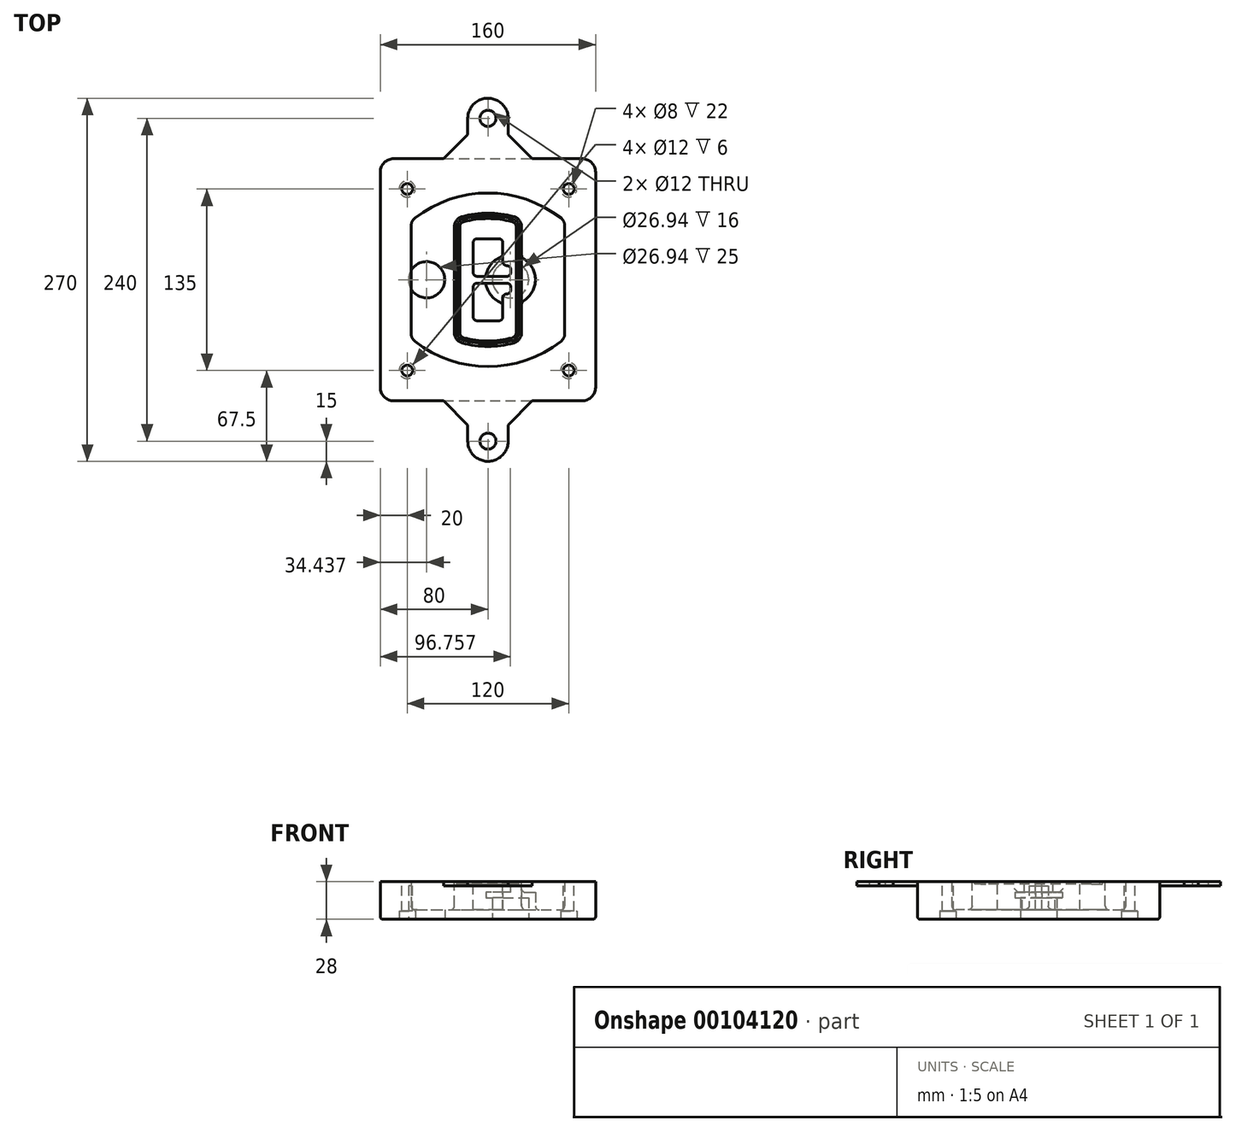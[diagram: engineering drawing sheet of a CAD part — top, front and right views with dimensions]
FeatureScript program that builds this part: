
annotation { "Feature Type Name" : "Feature", "Feature Type Description" : "" }
export const myFeature = defineFeature(function(context is Context, id is Id, definition is map)
    precondition{}
    {
        {
            var Q0;
            Q0=qCreatedBy(makeId("Top.planeOp"),FACE);
            var sketch = newSketch(context, id + "F0", { "sketchPlane" : qUnion([Q0])});
            skPoint(sketch, "E0.rect.middle", {"position": v(0, 0) * mm});
            skLineSegment(sketch, "E1.bottom", {"start": v(-70, -90) * mm, "end": v(70, -90) * mm});
            skLineSegment(sketch, "E1.top", {"start": v(-70, 90) * mm, "end": v(70, 90) * mm});
            skLineSegment(sketch, "E1.left", {"start": v(-80, -80) * mm, "end": v(-80, 80) * mm});
            skLineSegment(sketch, "E1.right", {"start": v(80, -80) * mm, "end": v(80, 80) * mm});
            skLineSegment(sketch, "E2", {"start": v(-80, 90) * mm, "end": v(80, -90) * mm, "construction": true});
            skLineSegment(sketch, "E3", {"start": v(80, 90) * mm, "end": v(-80, -90) * mm, "construction": true});
            skCircle(sketch, "E4", {"center": v(-60, 67.5) * mm, "radius": 4 * mm});
            skCircle(sketch, "E5", {"center": v(60, 67.5) * mm, "radius": 4 * mm});
            skCircle(sketch, "E6", {"center": v(60, -67.5) * mm, "radius": 4 * mm});
            skCircle(sketch, "E7", {"center": v(-60, -67.5) * mm, "radius": 4 * mm});
            skLineSegment(sketch, "E8", {"start": v(-60, 67.5) * mm, "end": v(60, 67.5) * mm, "construction": true});
            skLineSegment(sketch, "E9", {"start": v(60, 67.5) * mm, "end": v(60, -67.5) * mm, "construction": true});
            skLineSegment(sketch, "E10", {"start": v(60, -67.5) * mm, "end": v(-60, -67.5) * mm, "construction": true});
            skLineSegment(sketch, "E11", {"start": v(-60, -67.5) * mm, "end": v(-60, 67.5) * mm, "construction": true});
            skLineSegment(sketch, "E12", {"start": v(-60, 40.3) * mm, "end": v(-60, -40.3) * mm});
            skLineSegment(sketch, "E13", {"start": v(60, 40.3) * mm, "end": v(60, -40.3) * mm});
            skArc(sketch, "E14", {"start": v(56.15, 48.18) * mm, "mid": v(0, 67.5) * mm, "end": v(-56.15, 48.18) * mm});
            skArc(sketch, "E15", {"start": v(-56.15, -48.18) * mm, "mid": v(0, -67.5) * mm, "end": v(56.15, -48.18) * mm});
            skLineSegment(sketch, "E16", {"start": v(-60, 0) * mm, "end": v(60, 0) * mm, "construction": true});
            skPoint(sketch, "E17.visualSharp", {"position": v(-60, -45) * mm});
            skArc(sketch, "E17.filletArc", {"start": v(-60, -40.3) * mm, "mid": v(-58.99, -44.68) * mm, "end": v(-56.15, -48.18) * mm});
            skPoint(sketch, "E18.visualSharp", {"position": v(-60, 45) * mm});
            skArc(sketch, "E18.filletArc", {"start": v(-56.15, 48.18) * mm, "mid": v(-58.99, 44.68) * mm, "end": v(-60, 40.3) * mm});
            skPoint(sketch, "E19.visualSharp", {"position": v(60, 45) * mm});
            skArc(sketch, "E19.filletArc", {"start": v(60, 40.3) * mm, "mid": v(58.99, 44.68) * mm, "end": v(56.15, 48.18) * mm});
            skPoint(sketch, "E20.visualSharp", {"position": v(60, -45) * mm});
            skArc(sketch, "E20.filletArc", {"start": v(56.15, -48.18) * mm, "mid": v(58.99, -44.68) * mm, "end": v(60, -40.3) * mm});
            skPoint(sketch, "E21.visualSharp", {"position": v(-80, 90) * mm});
            skArc(sketch, "E21.filletArc", {"start": v(-70, 90) * mm, "mid": v(-77.07, 87.07) * mm, "end": v(-80, 80) * mm});
            skPoint(sketch, "E22.visualSharp", {"position": v(80, 90) * mm});
            skArc(sketch, "E22.filletArc", {"start": v(80, 80) * mm, "mid": v(77.07, 87.07) * mm, "end": v(70, 90) * mm});
            skPoint(sketch, "E23.visualSharp", {"position": v(80, -90) * mm});
            skArc(sketch, "E23.filletArc", {"start": v(70, -90) * mm, "mid": v(77.07, -87.07) * mm, "end": v(80, -80) * mm});
            skPoint(sketch, "E24.visualSharp", {"position": v(-80, -90) * mm});
            skArc(sketch, "E24.filletArc", {"start": v(-80, -80) * mm, "mid": v(-77.07, -87.07) * mm, "end": v(-70, -90) * mm});
            skArc(sketch, "E25.0", {"start": v(57, 40.3) * mm, "mid": v(56.3, 43.36) * mm, "end": v(54.3, 45.81) * mm});
            skLineSegment(sketch, "E25.1", {"start": v(57, 40.3) * mm, "end": v(57, -40.3) * mm});
            skArc(sketch, "E25.2", {"start": v(54.3, -45.81) * mm, "mid": v(56.3, -43.36) * mm, "end": v(57, -40.3) * mm});
            skArc(sketch, "E25.3", {"start": v(-54.3, -45.81) * mm, "mid": v(0, -64.5) * mm, "end": v(54.3, -45.81) * mm});
            skArc(sketch, "E25.4", {"start": v(-57, -40.3) * mm, "mid": v(-56.3, -43.36) * mm, "end": v(-54.3, -45.81) * mm});
            skArc(sketch, "E25.5", {"start": v(54.3, 45.81) * mm, "mid": v(0, 64.5) * mm, "end": v(-54.3, 45.81) * mm});
            skLineSegment(sketch, "E25.6", {"start": v(-57, 40.3) * mm, "end": v(-57, -40.3) * mm});
            skArc(sketch, "E25.7", {"start": v(-54.3, 45.81) * mm, "mid": v(-56.3, 43.36) * mm, "end": v(-57, 40.3) * mm});
            skArc(sketch, "E26.0", {"start": v(-58.62, 51.33) * mm, "mid": v(-62.58, 46.43) * mm, "end": v(-64, 40.3) * mm});
            skArc(sketch, "E26.1", {"start": v(58.62, 51.33) * mm, "mid": v(0, 71.5) * mm, "end": v(-58.62, 51.33) * mm});
            skArc(sketch, "E26.2", {"start": v(64, 40.3) * mm, "mid": v(62.58, 46.43) * mm, "end": v(58.62, 51.33) * mm});
            skLineSegment(sketch, "E26.3", {"start": v(64, 40.3) * mm, "end": v(64, -40.3) * mm});
            skArc(sketch, "E26.4", {"start": v(58.62, -51.33) * mm, "mid": v(62.58, -46.43) * mm, "end": v(64, -40.3) * mm});
            skLineSegment(sketch, "E26.5", {"start": v(-64, 40.3) * mm, "end": v(-64, -40.3) * mm});
            skArc(sketch, "E26.6", {"start": v(-58.62, -51.33) * mm, "mid": v(0, -71.5) * mm, "end": v(58.62, -51.33) * mm});
            skArc(sketch, "E26.7", {"start": v(-64, -40.3) * mm, "mid": v(-62.58, -46.43) * mm, "end": v(-58.62, -51.33) * mm});
            skSolve(sketch);
        }
        {
            var Q0;
            Q0=makeQuery(id+"F0.imprint","IMPRINT",FACE,{"disambiguationData":[TD([[makeQuery(id+"F0.imprint","IMPRINT",EDGE,{"derivedFrom":sQuery(id+"F0.wireOp",EDGE,"E1.bottom")}),1.0]])]});
            var Q1;
            Q1=makeQuery(id+"F0.imprint","IMPRINT",FACE,{"disambiguationData":[TD([[makeQuery(id+"F0.imprint","IMPRINT",EDGE,{"derivedFrom":sQuery(id+"F0.wireOp",EDGE,"E12")}),1.0]])]});
            var Q2;
            Q2=makeQuery(id+"F0.imprint","IMPRINT",FACE,{"disambiguationData":[TD([[makeQuery(id+"F0.imprint","IMPRINT",EDGE,{"derivedFrom":sQuery(id+"F0.wireOp",EDGE,"E25.0")}),1.0]])]});
            var Q3;
            Q3=makeQuery(id+"F0.imprint","IMPRINT",FACE,{"disambiguationData":[TD([[makeQuery(id+"F0.imprint","IMPRINT",EDGE,{"derivedFrom":sQuery(id+"F0.wireOp",EDGE,"E12")}),-1.0]])]});
            extrude(context, id + "F1", {"entities" : qUnion([Q0, Q1, Q2, Q3]), "oppositeDirection" : true, "depth" : 25 * mm});
        }
        {
            var Q0;
            Q0=makeQuery(id+"F0.imprint","IMPRINT",FACE,{"disambiguationData":[TD([[makeQuery(id+"F0.imprint","IMPRINT",EDGE,{"derivedFrom":sQuery(id+"F0.wireOp",EDGE,"E12")}),1.0]])]});
            extrude(context, id + "F2", {"entities" : qUnion([Q0]), "operationType" : NewBodyOperationType.ADD, "depth" : 3 * mm});
        }
        {
            var Q0;
            Q0=makeQuery(id+"F0.imprint","IMPRINT",FACE,{"disambiguationData":[TD([[makeQuery(id+"F0.imprint","IMPRINT",EDGE,{"derivedFrom":sQuery(id+"F0.wireOp",EDGE,"E25.0")}),1.0]])]});
            extrude(context, id + "F3", {"entities" : qUnion([Q0]), "operationType" : NewBodyOperationType.REMOVE, "oppositeDirection" : true, "depth" : 18 * mm});
        }
        {
            var Q0;
            Q0=makeQuery(id+"F2.opExtrude","CAP_FACE",FACE,{"disambiguationData":[OSD([sQuery(id+"F0.wireOp",EDGE,"E12"),sQuery(id+"F0.wireOp",EDGE,"E13"),sQuery(id+"F0.wireOp",EDGE,"E14"),sQuery(id+"F0.wireOp",EDGE,"E15"),sQuery(id+"F0.wireOp",EDGE,"E17.filletArc"),sQuery(id+"F0.wireOp",EDGE,"E18.filletArc"),sQuery(id+"F0.wireOp",EDGE,"E19.filletArc"),sQuery(id+"F0.wireOp",EDGE,"E20.filletArc"),sQuery(id+"F0.wireOp",EDGE,"E25.0"),sQuery(id+"F0.wireOp",EDGE,"E25.1"),sQuery(id+"F0.wireOp",EDGE,"E25.2"),sQuery(id+"F0.wireOp",EDGE,"E25.3"),sQuery(id+"F0.wireOp",EDGE,"E25.4"),sQuery(id+"F0.wireOp",EDGE,"E25.5"),sQuery(id+"F0.wireOp",EDGE,"E25.6"),sQuery(id+"F0.wireOp",EDGE,"E25.7")])],"isStart":false});
            var sketch = newSketch(context, id + "F4", { "sketchPlane" : qUnion([Q0])});
            skArc(sketch, "E27.0", {"start": v(-19.08, -46.97) * mm, "mid": v(0, -49.5) * mm, "end": v(19.08, -46.97) * mm});
            skArc(sketch, "E28.0", {"start": v(19.08, 46.97) * mm, "mid": v(0, 49.5) * mm, "end": v(-19.08, 46.97) * mm});
            skLineSegment(sketch, "E29", {"start": v(-25, 39.25) * mm, "end": v(-25, -39.25) * mm});
            skLineSegment(sketch, "E30", {"start": v(25, 39.25) * mm, "end": v(25, -39.25) * mm});
            skLineSegment(sketch, "E31", {"start": v(-25, 45.1) * mm, "end": v(25, 45.1) * mm, "construction": true});
            skLineSegment(sketch, "E32", {"start": v(-25, -45.1) * mm, "end": v(25, -45.1) * mm, "construction": true});
            skPoint(sketch, "E33.visualSharp", {"position": v(-25, 45.1) * mm});
            skArc(sketch, "E33.filletArc", {"start": v(-19.08, 46.97) * mm, "mid": v(-23.35, 44.11) * mm, "end": v(-25, 39.25) * mm});
            skPoint(sketch, "E34.visualSharp", {"position": v(25, 45.1) * mm});
            skArc(sketch, "E34.filletArc", {"start": v(25, 39.25) * mm, "mid": v(23.35, 44.11) * mm, "end": v(19.08, 46.97) * mm});
            skPoint(sketch, "E35.visualSharp", {"position": v(25, -45.1) * mm});
            skArc(sketch, "E35.filletArc", {"start": v(19.08, -46.97) * mm, "mid": v(23.35, -44.11) * mm, "end": v(25, -39.25) * mm});
            skPoint(sketch, "E36.visualSharp", {"position": v(-25, -45.1) * mm});
            skArc(sketch, "E36.filletArc", {"start": v(-25, -39.25) * mm, "mid": v(-23.35, -44.11) * mm, "end": v(-19.08, -46.97) * mm});
            skArc(sketch, "E37.0", {"start": v(54.3, 45.81) * mm, "mid": v(0, 64.5) * mm, "end": v(-54.3, 45.81) * mm});
            skArc(sketch, "E37.1", {"start": v(-54.3, 45.81) * mm, "mid": v(-56.3, 43.36) * mm, "end": v(-57, 40.3) * mm});
            skLineSegment(sketch, "E37.2", {"start": v(-57, 40.3) * mm, "end": v(-57, -40.3) * mm});
            skArc(sketch, "E37.3", {"start": v(-57, -40.3) * mm, "mid": v(-56.3, -43.36) * mm, "end": v(-54.3, -45.81) * mm});
            skArc(sketch, "E37.4", {"start": v(-54.3, -45.81) * mm, "mid": v(0, -64.5) * mm, "end": v(54.3, -45.81) * mm});
            skArc(sketch, "E37.5", {"start": v(54.3, -45.81) * mm, "mid": v(56.3, -43.36) * mm, "end": v(57, -40.3) * mm});
            skLineSegment(sketch, "E37.6", {"start": v(57, 40.3) * mm, "end": v(57, -40.3) * mm});
            skArc(sketch, "E37.7", {"start": v(57, 40.3) * mm, "mid": v(56.3, 43.36) * mm, "end": v(54.3, 45.81) * mm});
            skLineSegment(sketch, "E38.0", {"start": v(23, 39.25) * mm, "end": v(23, -39.25) * mm});
            skArc(sketch, "E38.1", {"start": v(18.56, -45.04) * mm, "mid": v(21.76, -42.9) * mm, "end": v(23, -39.25) * mm});
            skArc(sketch, "E38.2", {"start": v(-18.56, -45.04) * mm, "mid": v(0, -47.5) * mm, "end": v(18.56, -45.04) * mm});
            skArc(sketch, "E38.3", {"start": v(-23, -39.25) * mm, "mid": v(-21.76, -42.9) * mm, "end": v(-18.56, -45.04) * mm});
            skLineSegment(sketch, "E38.4", {"start": v(-23, 39.25) * mm, "end": v(-23, -39.25) * mm});
            skArc(sketch, "E38.5", {"start": v(23, 39.25) * mm, "mid": v(21.76, 42.9) * mm, "end": v(18.56, 45.04) * mm});
            skArc(sketch, "E38.6", {"start": v(-18.56, 45.04) * mm, "mid": v(-21.76, 42.9) * mm, "end": v(-23, 39.25) * mm});
            skArc(sketch, "E38.7", {"start": v(18.56, 45.04) * mm, "mid": v(0, 47.5) * mm, "end": v(-18.56, 45.04) * mm});
            skArc(sketch, "E39.0", {"start": v(21, 39.25) * mm, "mid": v(20.18, 41.68) * mm, "end": v(18.04, 43.1) * mm});
            skLineSegment(sketch, "E39.1", {"start": v(21, 39.25) * mm, "end": v(21, -39.25) * mm});
            skArc(sketch, "E39.2", {"start": v(18.04, -43.1) * mm, "mid": v(20.18, -41.68) * mm, "end": v(21, -39.25) * mm});
            skArc(sketch, "E39.3", {"start": v(-18.04, -43.1) * mm, "mid": v(0, -45.5) * mm, "end": v(18.04, -43.1) * mm});
            skArc(sketch, "E39.4", {"start": v(-21, -39.25) * mm, "mid": v(-20.18, -41.68) * mm, "end": v(-18.04, -43.1) * mm});
            skArc(sketch, "E39.5", {"start": v(18.04, 43.1) * mm, "mid": v(0, 45.5) * mm, "end": v(-18.04, 43.1) * mm});
            skLineSegment(sketch, "E39.6", {"start": v(-21, 39.25) * mm, "end": v(-21, -39.25) * mm});
            skArc(sketch, "E39.7", {"start": v(-18.04, 43.1) * mm, "mid": v(-20.18, 41.68) * mm, "end": v(-21, 39.25) * mm});
            skLineSegment(sketch, "E40", {"start": v(-25, 0) * mm, "end": v(25, 0) * mm, "construction": true});
            skLineSegment(sketch, "E41", {"start": v(-11, 5.5) * mm, "end": v(-11, 27.5) * mm});
            skLineSegment(sketch, "E42", {"start": v(-8, 30.5) * mm, "end": v(8, 30.5) * mm});
            skLineSegment(sketch, "E43", {"start": v(11, 27.5) * mm, "end": v(11, 13.5) * mm});
            skLineSegment(sketch, "E44", {"start": v(14, 10.5) * mm, "end": v(14, 10.5) * mm});
            skLineSegment(sketch, "E45", {"start": v(17, 7.5) * mm, "end": v(17, 5.5) * mm});
            skLineSegment(sketch, "E46", {"start": v(14, 2.5) * mm, "end": v(-8, 2.5) * mm});
            skPoint(sketch, "E47.visualSharp", {"position": v(-11, 30.5) * mm});
            skArc(sketch, "E47.filletArc", {"start": v(-8, 30.5) * mm, "mid": v(-10.12, 29.62) * mm, "end": v(-11, 27.5) * mm});
            skPoint(sketch, "E48.visualSharp", {"position": v(11, 30.5) * mm});
            skArc(sketch, "E48.filletArc", {"start": v(11, 27.5) * mm, "mid": v(10.12, 29.62) * mm, "end": v(8, 30.5) * mm});
            skPoint(sketch, "E49.visualSharp", {"position": v(11, 10.5) * mm});
            skArc(sketch, "E49.filletArc", {"start": v(11, 13.5) * mm, "mid": v(11.88, 11.38) * mm, "end": v(14, 10.5) * mm});
            skPoint(sketch, "E50.visualSharp", {"position": v(17, 10.5) * mm});
            skArc(sketch, "E50.filletArc", {"start": v(17, 7.5) * mm, "mid": v(16.12, 9.62) * mm, "end": v(14, 10.5) * mm});
            skPoint(sketch, "E51.visualSharp", {"position": v(17, 2.5) * mm});
            skArc(sketch, "E51.filletArc", {"start": v(14, 2.5) * mm, "mid": v(16.12, 3.38) * mm, "end": v(17, 5.5) * mm});
            skPoint(sketch, "E52.visualSharp", {"position": v(-11, 2.5) * mm});
            skArc(sketch, "E52.filletArc", {"start": v(-11, 5.5) * mm, "mid": v(-10.12, 3.38) * mm, "end": v(-8, 2.5) * mm});
            skLineSegment(sketch, "E53.0.MirrorCS", {"start": v(14, -2.5) * mm, "end": v(-8, -2.5) * mm});
            skArc(sketch, "E54.0.MirrorCS", {"start": v(-11, -5.5) * mm, "mid": v(-10.12, -3.38) * mm, "end": v(-8, -2.5) * mm});
            skLineSegment(sketch, "E55.0.MirrorCS", {"start": v(-11, -5.5) * mm, "end": v(-11, -27.5) * mm});
            skArc(sketch, "E56.0.MirrorCS", {"start": v(-8, -30.5) * mm, "mid": v(-10.12, -29.62) * mm, "end": v(-11, -27.5) * mm});
            skLineSegment(sketch, "E57.0.MirrorCS", {"start": v(-8, -30.5) * mm, "end": v(8, -30.5) * mm});
            skArc(sketch, "E58.0.MirrorCS", {"start": v(11, -27.5) * mm, "mid": v(10.12, -29.62) * mm, "end": v(8, -30.5) * mm});
            skLineSegment(sketch, "E59.0.MirrorCS", {"start": v(11, -27.5) * mm, "end": v(11, -13.5) * mm});
            skArc(sketch, "E60.0.MirrorCS", {"start": v(11, -13.5) * mm, "mid": v(11.88, -11.38) * mm, "end": v(14, -10.5) * mm});
            skArc(sketch, "E61.0.MirrorCS", {"start": v(17, -7.5) * mm, "mid": v(16.12, -9.62) * mm, "end": v(14, -10.5) * mm});
            skLineSegment(sketch, "E62.0.MirrorCS", {"start": v(17, -7.5) * mm, "end": v(17, -5.5) * mm});
            skArc(sketch, "E63.0.MirrorCS", {"start": v(14, -2.5) * mm, "mid": v(16.12, -3.38) * mm, "end": v(17, -5.5) * mm});
            skSolve(sketch);
        }
        {
            var Q0;
            Q0=makeQuery(id+"F4.imprint","IMPRINT",FACE,{"disambiguationData":[TD([[makeQuery(id+"F4.imprint","IMPRINT",EDGE,{"derivedFrom":sQuery(id+"F4.wireOp",EDGE,"E27.0")}),1.0]])]});
            var Q1;
            Q1=makeQuery(id+"F4.imprint","IMPRINT",FACE,{"disambiguationData":[TD([[makeQuery(id+"F4.imprint","IMPRINT",EDGE,{"derivedFrom":sQuery(id+"F4.wireOp",EDGE,"E38.0")}),-1.0]])]});
            var Q2;
            Q2=makeQuery(id+"F4.imprint","IMPRINT",FACE,{"disambiguationData":[TD([[makeQuery(id+"F4.imprint","IMPRINT",EDGE,{"derivedFrom":sQuery(id+"F4.wireOp",EDGE,"E39.0")}),1.0]])]});
            extrude(context, id + "F5", {"entities" : qUnion([Q0, Q1, Q2]), "operationType" : NewBodyOperationType.ADD, "endBound" : BoundingType.UP_TO_NEXT, "oppositeDirection" : true, "depth" : 25 * mm});
        }
        {
            var Q0;
            Q0=makeQuery(id+"F4.imprint","IMPRINT",FACE,{"disambiguationData":[TD([[makeQuery(id+"F4.imprint","IMPRINT",EDGE,{"derivedFrom":sQuery(id+"F4.wireOp",EDGE,"E38.0")}),-1.0]])]});
            extrude(context, id + "F6", {"entities" : qUnion([Q0]), "operationType" : NewBodyOperationType.REMOVE, "oppositeDirection" : true, "depth" : 2 * mm});
        }
        {
            var Q0;
            Q0=makeQuery(id+"F1.opExtrude","CAP_FACE",FACE,{"disambiguationData":[OSD([sQuery(id+"F0.wireOp",EDGE,"E1.bottom"),sQuery(id+"F0.wireOp",EDGE,"E1.top"),sQuery(id+"F0.wireOp",EDGE,"E1.left"),sQuery(id+"F0.wireOp",EDGE,"E1.right"),sQuery(id+"F0.wireOp",EDGE,"E4"),sQuery(id+"F0.wireOp",EDGE,"E5"),sQuery(id+"F0.wireOp",EDGE,"E6"),sQuery(id+"F0.wireOp",EDGE,"E7"),sQuery(id+"F0.wireOp",EDGE,"E21.filletArc"),sQuery(id+"F0.wireOp",EDGE,"E22.filletArc"),sQuery(id+"F0.wireOp",EDGE,"E23.filletArc"),sQuery(id+"F0.wireOp",EDGE,"E24.filletArc")])],"isStart":false});
            var sketch = newSketch(context, id + "F7", { "sketchPlane" : qUnion([Q0])});
            skCircle(sketch, "E64", {"center": v(16.76, 0) * mm, "radius": 13.47 * mm});
            skCircle(sketch, "E65", {"center": v(-45.56, 0) * mm, "radius": 13.47 * mm});
            skLineSegment(sketch, "E66", {"start": v(80, 0) * mm, "end": v(-80, 0) * mm});
            skCircle(sketch, "E67", {"center": v(16.76, 0) * mm, "radius": 18.47 * mm});
            skCircle(sketch, "E68", {"center": v(60, -67.5) * mm, "radius": 6 * mm});
            skCircle(sketch, "E69", {"center": v(-60, -67.5) * mm, "radius": 6 * mm});
            skCircle(sketch, "E70", {"center": v(-60, 67.5) * mm, "radius": 6 * mm});
            skCircle(sketch, "E71", {"center": v(60, 67.5) * mm, "radius": 6 * mm});
            skSolve(sketch);
        }
        {
            var Q0;
            {var subQ1=sQuery(id+"F7.wireOp",EDGE,"E66");var subQ4=sQuery(id+"F7.wireOp",EDGE,"E64");var subQ6=makeQuery(id+"F7.imprint","INTERSECT",VERTEX,{"disambiguationData":[OD(0.0)],"derivedFrom":[subQ4,subQ1]});Q0=makeQuery(id+"F7.imprint","IMPRINT",FACE,{"disambiguationData":[TD([[makeQuery(id+"F7.imprint","IMPRINT",EDGE,{"disambiguationData":[TD([[subQ6,-1.0]])],"derivedFrom":subQ4}),-1.0]])]});}
            var Q1;
            {var subQ0=sQuery(id+"F7.wireOp",EDGE,"E66");var subQ1=sQuery(id+"F7.wireOp",EDGE,"E64");var subQ3=makeQuery(id+"F7.imprint","INTERSECT",VERTEX,{"disambiguationData":[OD(0.0)],"derivedFrom":[subQ1,subQ0]});Q1=makeQuery(id+"F7.imprint","IMPRINT",FACE,{"disambiguationData":[TD([[makeQuery(id+"F7.imprint","IMPRINT",EDGE,{"disambiguationData":[TD([[subQ3,-1.0]])],"derivedFrom":subQ1}),1.0]])]});}
            var Q2;
            {var subQ0=sQuery(id+"F7.wireOp",EDGE,"E66");var subQ1=sQuery(id+"F7.wireOp",EDGE,"E64");var subQ3=makeQuery(id+"F7.imprint","INTERSECT",VERTEX,{"disambiguationData":[OD(0.0)],"derivedFrom":[subQ1,subQ0]});Q2=makeQuery(id+"F7.imprint","IMPRINT",FACE,{"disambiguationData":[TD([[makeQuery(id+"F7.imprint","IMPRINT",EDGE,{"disambiguationData":[TD([[subQ3,1.0]])],"derivedFrom":subQ1}),1.0]])]});}
            var Q3;
            {var subQ1=sQuery(id+"F7.wireOp",EDGE,"E66");var subQ4=sQuery(id+"F7.wireOp",EDGE,"E64");var subQ6=makeQuery(id+"F7.imprint","INTERSECT",VERTEX,{"disambiguationData":[OD(0.0)],"derivedFrom":[subQ4,subQ1]});Q3=makeQuery(id+"F7.imprint","IMPRINT",FACE,{"disambiguationData":[TD([[makeQuery(id+"F7.imprint","IMPRINT",EDGE,{"disambiguationData":[TD([[subQ6,1.0]])],"derivedFrom":subQ4}),-1.0]])]});}
            extrude(context, id + "F8", {"entities" : qUnion([Q0, Q1, Q2, Q3]), "operationType" : NewBodyOperationType.ADD, "oppositeDirection" : true, "depth" : 20 * mm});
        }
        {
            var Q0;
            {var subQ0=sQuery(id+"F7.wireOp",EDGE,"E66");var subQ1=sQuery(id+"F7.wireOp",EDGE,"E64");var subQ3=makeQuery(id+"F7.imprint","INTERSECT",VERTEX,{"disambiguationData":[OD(0.0)],"derivedFrom":[subQ1,subQ0]});Q0=makeQuery(id+"F7.imprint","IMPRINT",FACE,{"disambiguationData":[TD([[makeQuery(id+"F7.imprint","IMPRINT",EDGE,{"disambiguationData":[TD([[subQ3,-1.0]])],"derivedFrom":subQ1}),1.0]])]});}
            var Q1;
            {var subQ0=sQuery(id+"F7.wireOp",EDGE,"E66");var subQ1=sQuery(id+"F7.wireOp",EDGE,"E64");var subQ3=makeQuery(id+"F7.imprint","INTERSECT",VERTEX,{"disambiguationData":[OD(0.0)],"derivedFrom":[subQ1,subQ0]});Q1=makeQuery(id+"F7.imprint","IMPRINT",FACE,{"disambiguationData":[TD([[makeQuery(id+"F7.imprint","IMPRINT",EDGE,{"disambiguationData":[TD([[subQ3,1.0]])],"derivedFrom":subQ1}),1.0]])]});}
            extrude(context, id + "F9", {"entities" : qUnion([Q0, Q1]), "operationType" : NewBodyOperationType.REMOVE, "oppositeDirection" : true, "depth" : 16 * mm});
        }
        {
            var Q0;
            {var subQ0=sQuery(id+"F7.wireOp",EDGE,"E66");var subQ1=sQuery(id+"F7.wireOp",EDGE,"E65");var subQ3=makeQuery(id+"F7.imprint","INTERSECT",VERTEX,{"disambiguationData":[OD(0.0)],"derivedFrom":[subQ1,subQ0]});Q0=makeQuery(id+"F7.imprint","IMPRINT",FACE,{"disambiguationData":[TD([[makeQuery(id+"F7.imprint","IMPRINT",EDGE,{"disambiguationData":[TD([[subQ3,-1.0]])],"derivedFrom":subQ1}),1.0]])]});}
            var Q1;
            {var subQ0=sQuery(id+"F7.wireOp",EDGE,"E66");var subQ1=sQuery(id+"F7.wireOp",EDGE,"E65");var subQ3=makeQuery(id+"F7.imprint","INTERSECT",VERTEX,{"disambiguationData":[OD(0.0)],"derivedFrom":[subQ1,subQ0]});Q1=makeQuery(id+"F7.imprint","IMPRINT",FACE,{"disambiguationData":[TD([[makeQuery(id+"F7.imprint","IMPRINT",EDGE,{"disambiguationData":[TD([[subQ3,1.0]])],"derivedFrom":subQ1}),1.0]])]});}
            extrude(context, id + "F10", {"entities" : qUnion([Q0, Q1]), "operationType" : NewBodyOperationType.REMOVE, "oppositeDirection" : true, "depth" : 25 * mm});
        }
        {
            var Q0;
            Q0=makeQuery(id+"F7.imprint","IMPRINT",FACE,{"disambiguationData":[TD([[makeQuery(id+"F7.imprint","IMPRINT",EDGE,{"derivedFrom":sQuery(id+"F7.wireOp",EDGE,"E68")}),1.0]])]});
            var Q1;
            Q1=makeQuery(id+"F7.imprint","IMPRINT",FACE,{"disambiguationData":[TD([[makeQuery(id+"F7.imprint","IMPRINT",EDGE,{"derivedFrom":makeQuery(id+"F1.opExtrude","CAP_EDGE",EDGE,{"disambiguationData":[OSD([sQuery(id+"F0.wireOp",EDGE,"E5")])],"isStart":false})}),-1.0]])]});
            var Q2;
            Q2=makeQuery(id+"F7.imprint","IMPRINT",FACE,{"disambiguationData":[TD([[makeQuery(id+"F7.imprint","IMPRINT",EDGE,{"derivedFrom":sQuery(id+"F7.wireOp",EDGE,"E69")}),1.0]])]});
            var Q3;
            Q3=makeQuery(id+"F7.imprint","IMPRINT",FACE,{"disambiguationData":[TD([[makeQuery(id+"F7.imprint","IMPRINT",EDGE,{"derivedFrom":makeQuery(id+"F1.opExtrude","CAP_EDGE",EDGE,{"disambiguationData":[OSD([sQuery(id+"F0.wireOp",EDGE,"E4")])],"isStart":false})}),-1.0]])]});
            var Q4;
            Q4=makeQuery(id+"F7.imprint","IMPRINT",FACE,{"disambiguationData":[TD([[makeQuery(id+"F7.imprint","IMPRINT",EDGE,{"derivedFrom":sQuery(id+"F7.wireOp",EDGE,"E70")}),1.0]])]});
            var Q5;
            Q5=makeQuery(id+"F7.imprint","IMPRINT",FACE,{"disambiguationData":[TD([[makeQuery(id+"F7.imprint","IMPRINT",EDGE,{"derivedFrom":makeQuery(id+"F1.opExtrude","CAP_EDGE",EDGE,{"disambiguationData":[OSD([sQuery(id+"F0.wireOp",EDGE,"E7")])],"isStart":false})}),-1.0]])]});
            var Q6;
            Q6=makeQuery(id+"F7.imprint","IMPRINT",FACE,{"disambiguationData":[TD([[makeQuery(id+"F7.imprint","IMPRINT",EDGE,{"derivedFrom":sQuery(id+"F7.wireOp",EDGE,"E71")}),1.0]])]});
            var Q7;
            Q7=makeQuery(id+"F7.imprint","IMPRINT",FACE,{"disambiguationData":[TD([[makeQuery(id+"F7.imprint","IMPRINT",EDGE,{"derivedFrom":makeQuery(id+"F1.opExtrude","CAP_EDGE",EDGE,{"disambiguationData":[OSD([sQuery(id+"F0.wireOp",EDGE,"E6")])],"isStart":false})}),-1.0]])]});
            extrude(context, id + "F11", {"entities" : qUnion([Q0, Q1, Q2, Q3, Q4, Q5, Q6, Q7]), "operationType" : NewBodyOperationType.REMOVE, "oppositeDirection" : true, "depth" : 6 * mm});
        }
        {
            var Q0;
            Q0=makeQuery(id+"F9.boolean.opBoolean","COPY",FACE,{"derivedFrom":makeQuery(id+"F9.opExtrude","CAP_FACE",FACE,{"disambiguationData":[OSD([sQuery(id+"F7.wireOp",EDGE,"E64")])],"isStart":false})});
            var sketch = newSketch(context, id + "F12", { "sketchPlane" : qUnion([Q0])});
            skArc(sketch, "E72.0", {"start": v(11, 17.55) * mm, "mid": v(2.57, 11.82) * mm, "end": v(-1.54, 2.5) * mm});
            skArc(sketch, "E72.1", {"start": v(-1.54, -2.5) * mm, "mid": v(2.57, -11.82) * mm, "end": v(11, -17.55) * mm});
            skLineSegment(sketch, "E73", {"start": v(-1.54, -2.5) * mm, "end": v(14, -2.5) * mm});
            skLineSegment(sketch, "E74.0", {"start": v(14, 2.5) * mm, "end": v(-1.54, 2.5) * mm});
            skArc(sketch, "E74.1", {"start": v(14, 2.5) * mm, "mid": v(16.12, 3.38) * mm, "end": v(17, 5.5) * mm});
            skLineSegment(sketch, "E74.2", {"start": v(17, 7.5) * mm, "end": v(17, 5.5) * mm});
            skArc(sketch, "E74.3", {"start": v(17, 7.5) * mm, "mid": v(16.12, 9.62) * mm, "end": v(14, 10.5) * mm});
            skArc(sketch, "E74.4", {"start": v(11, 13.5) * mm, "mid": v(11.88, 11.38) * mm, "end": v(14, 10.5) * mm});
            skLineSegment(sketch, "E74.5", {"start": v(11, 17.55) * mm, "end": v(11, 13.5) * mm});
            skLineSegment(sketch, "E74.7", {"start": v(14, -2.5) * mm, "end": v(-1.54, -2.5) * mm});
            skArc(sketch, "E74.8", {"start": v(14, -2.5) * mm, "mid": v(16.12, -3.38) * mm, "end": v(17, -5.5) * mm});
            skLineSegment(sketch, "E74.9", {"start": v(17, -7.5) * mm, "end": v(17, -5.5) * mm});
            skArc(sketch, "E74.10", {"start": v(17, -7.5) * mm, "mid": v(16.12, -9.62) * mm, "end": v(14, -10.5) * mm});
            skArc(sketch, "E74.11", {"start": v(11, -13.5) * mm, "mid": v(11.88, -11.38) * mm, "end": v(14, -10.5) * mm});
            skLineSegment(sketch, "E74.12", {"start": v(11, -17.55) * mm, "end": v(11, -13.5) * mm});
            skPoint(sketch, "E75.orphan", {"position": v(11, -27.5) * mm});
            skPoint(sketch, "E76.orphan", {"position": v(-8, -2.5) * mm});
            skPoint(sketch, "E77.orphan", {"position": v(-8, 2.5) * mm});
            skPoint(sketch, "E78.orphan", {"position": v(11, 27.5) * mm});
            skSolve(sketch);
        }
        {
            var Q0;
            {var subQ7=sQuery(id+"F12.wireOp",EDGE,"E72.0");var subQ14=sQuery(id+"F12.wireOp",EDGE,"E72.1");var subQ16=sQuery(id+"F12.wireOp",EDGE,"E74.1");var subQ18=sQuery(id+"F12.wireOp",EDGE,"E74.8");Q0=qUnion([makeQuery(id+"F12.imprint","IMPRINT",FACE,{"disambiguationData":[TD([[makeQuery(id+"F12.imprint","IMPRINT",EDGE,{"derivedFrom":subQ7}),1.0]])]}),makeQuery(id+"F12.imprint","IMPRINT",FACE,{"disambiguationData":[TD([[makeQuery(id+"F12.imprint","IMPRINT",EDGE,{"derivedFrom":subQ14}),1.0]])]}),makeQuery(id+"F12.imprint","IMPRINT",FACE,{"disambiguationData":[TD([[makeQuery(id+"F12.imprint","IMPRINT",EDGE,{"derivedFrom":subQ16}),1.0]])]}),makeQuery(id+"F12.imprint","IMPRINT",FACE,{"disambiguationData":[TD([[makeQuery(id+"F12.imprint","IMPRINT",EDGE,{"derivedFrom":subQ18}),-1.0]])]})]);}
            var Q1;
            Q1=makeQuery(id+"F5.boolean.opBoolean","SPLIT",FACE,{"disambiguationData":[TD([makeQuery(id+"F5.opExtrude","SWEPT_FACE",FACE,{"disambiguationData":[OSD([sQuery(id+"F4.wireOp",EDGE,"E41")])]})])],"derivedFrom":makeQuery(id+"F3.boolean.opBoolean","COPY",FACE,{"derivedFrom":makeQuery(id+"F3.opExtrude","CAP_FACE",FACE,{"disambiguationData":[OSD([sQuery(id+"F0.wireOp",EDGE,"E25.0"),sQuery(id+"F0.wireOp",EDGE,"E25.1"),sQuery(id+"F0.wireOp",EDGE,"E25.2"),sQuery(id+"F0.wireOp",EDGE,"E25.3"),sQuery(id+"F0.wireOp",EDGE,"E25.4"),sQuery(id+"F0.wireOp",EDGE,"E25.5"),sQuery(id+"F0.wireOp",EDGE,"E25.6"),sQuery(id+"F0.wireOp",EDGE,"E25.7")])],"isStart":false})})});
            extrude(context, id + "F13", {"entities" : qUnion([Q0]), "operationType" : NewBodyOperationType.REMOVE, "endBound" : BoundingType.UP_TO_SURFACE, "endBoundEntityFace" : qUnion([Q1]), "depth" : 25 * mm});
        }
        {
            var Q0;
            Q0=makeQuery(id+"F3.boolean.opBoolean","COPY",EDGE,{"derivedFrom":makeQuery(id+"F3.opExtrude","CAP_EDGE",EDGE,{"disambiguationData":[OSD([sQuery(id+"F0.wireOp",EDGE,"E25.6")])],"isStart":false})});
            var Q1;
            Q1=makeQuery(id+"F8.boolean.opBoolean","INTERSECT",EDGE,{"derivedFrom":[makeQuery(id+"F5.opExtrude","SWEPT_FACE",FACE,{"disambiguationData":[OSD([sQuery(id+"F4.wireOp",EDGE,"E30")])]}),makeQuery(id+"F8.opExtrude","CAP_FACE",FACE,{"disambiguationData":[OSD([sQuery(id+"F7.wireOp",EDGE,"E67")])],"isStart":false})]});
            var Q2;
            Q2=makeQuery(id+"F8.boolean.opBoolean","INTERSECT",EDGE,{"disambiguationData":[OD(1.0)],"derivedFrom":[makeQuery(id+"F5.opExtrude","SWEPT_FACE",FACE,{"disambiguationData":[OSD([sQuery(id+"F4.wireOp",EDGE,"E30")])]}),makeQuery(id+"F8.opExtrude","SWEPT_FACE",FACE,{"disambiguationData":[OSD([sQuery(id+"F7.wireOp",EDGE,"E67")])]})]});
            var Q3;
            {var subQ0=sQuery(id+"F4.wireOp",EDGE,"E30");Q3=makeQuery(id+"F8.boolean.opBoolean","SPLIT",EDGE,{"disambiguationData":[TD([makeQuery(id+"F5.opExtrude","SWEPT_FACE",FACE,{"disambiguationData":[OSD([sQuery(id+"F4.wireOp",EDGE,"E35.filletArc")])]})])],"derivedFrom":makeQuery(id+"F5.opExtrude","CAP_EDGE",EDGE,{"disambiguationData":[OSD([subQ0])],"isStart":false})});}
            var Q4;
            {var subQ0=sQuery(id+"F0.wireOp",EDGE,"E25.7");var subQ1=sQuery(id+"F0.wireOp",EDGE,"E25.1");var subQ2=sQuery(id+"F0.wireOp",EDGE,"E25.6");var subQ3=sQuery(id+"F0.wireOp",EDGE,"E25.5");var subQ4=sQuery(id+"F0.wireOp",EDGE,"E25.4");var subQ5=sQuery(id+"F0.wireOp",EDGE,"E25.0");var subQ6=sQuery(id+"F0.wireOp",EDGE,"E25.2");var subQ7=sQuery(id+"F0.wireOp",EDGE,"E25.3");Q4=makeQuery(id+"F8.boolean.opBoolean","INTERSECT",EDGE,{"derivedFrom":[makeQuery(id+"F5.boolean.opBoolean","SPLIT",FACE,{"disambiguationData":[TD([makeQuery(id+"F2.opExtrude","SWEPT_FACE",FACE,{"disambiguationData":[OSD([subQ5])]})])],"derivedFrom":makeQuery(id+"F3.boolean.opBoolean","COPY",FACE,{"derivedFrom":makeQuery(id+"F3.opExtrude","CAP_FACE",FACE,{"disambiguationData":[OSD([subQ5,subQ1,subQ6,subQ7,subQ4,subQ3,subQ2,subQ0])],"isStart":false})})}),makeQuery(id+"F8.opExtrude","SWEPT_FACE",FACE,{"disambiguationData":[OSD([sQuery(id+"F7.wireOp",EDGE,"E67")])]})]});}
            var Q5;
            Q5=makeQuery(id+"F8.boolean.opBoolean","INTERSECT",EDGE,{"disambiguationData":[OD(0.0)],"derivedFrom":[makeQuery(id+"F5.opExtrude","SWEPT_FACE",FACE,{"disambiguationData":[OSD([sQuery(id+"F4.wireOp",EDGE,"E30")])]}),makeQuery(id+"F8.opExtrude","SWEPT_FACE",FACE,{"disambiguationData":[OSD([sQuery(id+"F7.wireOp",EDGE,"E67")])]})]});
            fillet(context, id + "F14", {"entities" : qUnion([Q0, Q1, Q2, Q3, Q4, Q5]), "radius" : 3 * mm, "tangentPropagation" : true, "allowEdgeOverflow" : false});
        }
        {
            var Q0;
            Q0=makeQuery(id+"F1.opExtrude","CAP_EDGE",EDGE,{"disambiguationData":[OSD([sQuery(id+"F0.wireOp",EDGE,"E1.bottom")])],"isStart":false});
            fillet(context, id + "F15", {"entities" : qUnion([Q0]), "radius" : 2 * mm, "tangentPropagation" : true, "allowEdgeOverflow" : false});
        }
        {
            var Q0;
            {var subQ0=sQuery(id+"F0.wireOp",EDGE,"E22.filletArc");var subQ1=sQuery(id+"F0.wireOp",EDGE,"E7");var subQ2=sQuery(id+"F0.wireOp",EDGE,"E6");var subQ3=sQuery(id+"F0.wireOp",EDGE,"E5");var subQ4=sQuery(id+"F0.wireOp",EDGE,"E4");var subQ5=sQuery(id+"F0.wireOp",EDGE,"E1.bottom");var subQ6=sQuery(id+"F0.wireOp",EDGE,"E21.filletArc");var subQ7=sQuery(id+"F0.wireOp",EDGE,"E1.top");var subQ8=sQuery(id+"F0.wireOp",EDGE,"E1.left");var subQ9=sQuery(id+"F0.wireOp",EDGE,"E1.right");var subQ10=sQuery(id+"F0.wireOp",EDGE,"E23.filletArc");var subQ11=sQuery(id+"F0.wireOp",EDGE,"E24.filletArc");Q0=makeQuery(id+"F2.boolean.opBoolean","SPLIT",FACE,{"disambiguationData":[TD([makeQuery(id+"F1.opExtrude","SWEPT_FACE",FACE,{"disambiguationData":[OSD([subQ5])]})])],"derivedFrom":makeQuery(id+"F1.opExtrude","CAP_FACE",FACE,{"disambiguationData":[OSD([subQ5,subQ7,subQ8,subQ9,subQ4,subQ3,subQ2,subQ1,subQ6,subQ0,subQ10,subQ11])],"isStart":true})});}
            var sketch = newSketch(context, id + "F16", { "sketchPlane" : qUnion([Q0])});
            skLineSegment(sketch, "E79", {"start": v(-32.97, 90) * mm, "end": v(-14.97, 108) * mm});
            skLineSegment(sketch, "E80", {"start": v(-14.97, 108) * mm, "end": v(-14.97, 119.04) * mm});
            skLineSegment(sketch, "E81", {"start": v(32.92, 90) * mm, "end": v(14.92, 108) * mm});
            skLineSegment(sketch, "E82", {"start": v(14.92, 108) * mm, "end": v(14.92, 118.46) * mm});
            skArc(sketch, "E83", {"start": v(14.92, 118.46) * mm, "mid": v(0.29, 135) * mm, "end": v(-14.97, 119.04) * mm});
            skLineSegment(sketch, "E84", {"start": v(0, 90) * mm, "end": v(0, 120) * mm, "construction": true});
            skCircle(sketch, "E85", {"center": v(0, 120) * mm, "radius": 6 * mm});
            skLineSegment(sketch, "E86", {"start": v(-80, 0) * mm, "end": v(80, 0) * mm, "construction": true});
            skLineSegment(sketch, "E87.MirrorCS", {"start": v(-32.97, -90) * mm, "end": v(-14.97, -108) * mm});
            skLineSegment(sketch, "E88.MirrorCS", {"start": v(-14.97, -108) * mm, "end": v(-14.97, -119.04) * mm});
            skArc(sketch, "E89.MirrorCS", {"start": v(14.92, -118.46) * mm, "mid": v(0.29, -135) * mm, "end": v(-14.97, -119.04) * mm});
            skLineSegment(sketch, "E90.MirrorCS", {"start": v(14.92, -108) * mm, "end": v(14.92, -118.46) * mm});
            skLineSegment(sketch, "E91.MirrorCS", {"start": v(32.92, -90) * mm, "end": v(14.92, -108) * mm});
            skLineSegment(sketch, "E92.MirrorCS", {"start": v(0, -90) * mm, "end": v(0, -120) * mm, "construction": true});
            skCircle(sketch, "E93.MirrorC", {"center": v(0, -120) * mm, "radius": 6 * mm});
            skSolve(sketch);
        }
        {
            var Q0;
            {var subQ0=sQuery(id+"F16.wireOp",EDGE,"E87.MirrorCS");Q0=makeQuery(id+"F16.imprint","IMPRINT",FACE,{"disambiguationData":[TD([[makeQuery(id+"F16.imprint","IMPRINT",EDGE,{"derivedFrom":subQ0}),1.0]])]});}
            var Q1;
            Q1=makeQuery(id+"F16.imprint","IMPRINT",FACE,{"disambiguationData":[TD([[makeQuery(id+"F16.imprint","IMPRINT",EDGE,{"derivedFrom":makeQuery(id+"F1.opExtrude","CAP_EDGE",EDGE,{"disambiguationData":[OSD([sQuery(id+"F0.wireOp",EDGE,"E1.left")])],"isStart":true})}),-1.0]])]});
            var Q2;
            {var subQ1=sQuery(id+"F16.wireOp",EDGE,"E79");Q2=makeQuery(id+"F16.imprint","IMPRINT",FACE,{"disambiguationData":[TD([[makeQuery(id+"F16.imprint","IMPRINT",EDGE,{"derivedFrom":subQ1}),-1.0]])]});}
            var Q3;
            Q3=makeQuery(id+"F2.opExtrude","CAP_FACE",FACE,{"disambiguationData":[OSD([sQuery(id+"F0.wireOp",EDGE,"E12"),sQuery(id+"F0.wireOp",EDGE,"E13"),sQuery(id+"F0.wireOp",EDGE,"E14"),sQuery(id+"F0.wireOp",EDGE,"E15"),sQuery(id+"F0.wireOp",EDGE,"E17.filletArc"),sQuery(id+"F0.wireOp",EDGE,"E18.filletArc"),sQuery(id+"F0.wireOp",EDGE,"E19.filletArc"),sQuery(id+"F0.wireOp",EDGE,"E20.filletArc"),sQuery(id+"F0.wireOp",EDGE,"E25.0"),sQuery(id+"F0.wireOp",EDGE,"E25.1"),sQuery(id+"F0.wireOp",EDGE,"E25.2"),sQuery(id+"F0.wireOp",EDGE,"E25.3"),sQuery(id+"F0.wireOp",EDGE,"E25.4"),sQuery(id+"F0.wireOp",EDGE,"E25.5"),sQuery(id+"F0.wireOp",EDGE,"E25.6"),sQuery(id+"F0.wireOp",EDGE,"E25.7")])],"isStart":false});
            extrude(context, id + "F17", {"entities" : qUnion([Q0, Q1, Q2]), "operationType" : NewBodyOperationType.ADD, "endBound" : BoundingType.UP_TO_SURFACE, "endBoundEntityFace" : qUnion([Q3]), "depth" : 25 * mm});
        }
    });
